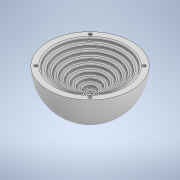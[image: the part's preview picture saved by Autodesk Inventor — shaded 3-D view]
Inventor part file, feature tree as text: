
AUTODESK INVENTOR PART (.ipt)
format: ipt  version: 2022 (Build 260153000, 153)  size: 421,376 bytes
history: native  units: mm
features: extrude x17, sketch x17, other x10, fillet x6
ambient origin geometry x8: Origin, YZ Plane, XZ Plane, XY Plane, X Axis, Y Axis, Z Axis, Center Point
bodies: Body1 (feature_tree)
feature tree (50):
  other  "實體1"
  extrude  "擠出1"  Depth=60.0mm
  fillet  "圓角1"  Radius=30.0mm
  extrude  "擠出2"  Depth=30.0mm
  extrude  "擠出3"  Depth=50.0mm
  extrude  "擠出4"  Depth=2.0mm TaperAngle=0.0deg
  extrude  "擠出5"  Depth=44.0mm
  extrude  "擠出6"  Depth=2.0mm TaperAngle=0.0deg
  extrude  "擠出7"  Depth=38.0mm
  extrude  "擠出8"  Depth=2.0mm TaperAngle=0.0deg
  extrude  "擠出9"  Depth=32.0mm
  extrude  "擠出11"  Depth=2.0mm TaperAngle=0.0deg
  extrude  "擠出12"  Depth=26.0mm
  extrude  "擠出13"  Depth=2.0mm TaperAngle=0.0deg
  extrude  "擠出16"  Depth=20.0mm
  fillet  "圓角2"  Radius=2.0mm
  extrude  "擠出17"  Depth=14.0mm
  fillet  "圓角3"  Radius=2.0mm
  extrude  "擠出18"  Depth=8.0mm
  fillet  "圓角4"  Radius=2.0mm
  extrude  "擠出19"  Depth=3.0mm
  fillet  "圓角5"  Radius=2.0mm
  other  "面圓角1"
  other  "面圓角2"
  other  "面圓角3"
  other  "面圓角4"
  other  "面圓角5"
  other  "面圓角6"
  other  "面圓角7"
  other  "面圓角8"
  extrude  "擠出20"  Depth=3.0mm
  other  "面圓角9"
  fillet  "圓角6"  Radius=50.0mm
  sketch  "草圖3"
  sketch  "草圖4"
  sketch  "草圖5"
  sketch  "草圖6"
  sketch  "草圖7"
  sketch  "草圖8"
  sketch  "草圖9"
  sketch  "草圖10"
  sketch  "草圖11"
  sketch  "草圖14"
  sketch  "草圖15"
  sketch  "草圖16"
  sketch  "草圖25"
  sketch  "草圖26"
  sketch  "草圖27"
  sketch  "草圖29"
  sketch  "草圖30"
